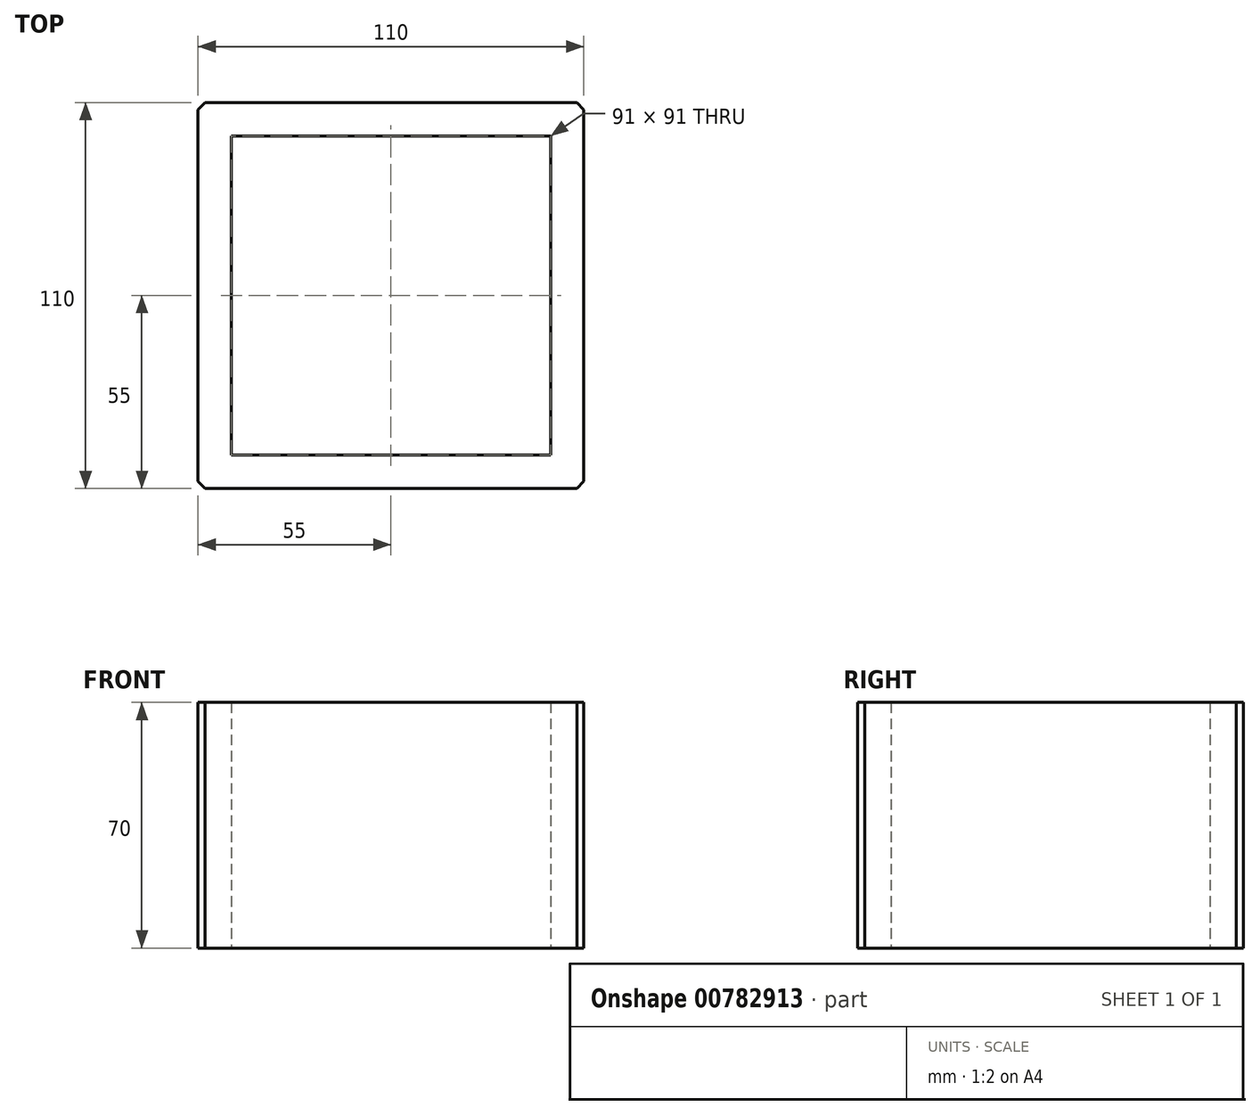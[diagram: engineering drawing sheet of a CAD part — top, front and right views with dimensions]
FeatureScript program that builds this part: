
annotation { "Feature Type Name" : "Feature", "Feature Type Description" : "" }
export const myFeature = defineFeature(function(context is Context, id is Id, definition is map)
    precondition{}
    {
        {
            var Q0;
            Q0=qCreatedBy(makeId("Top.planeOp"),FACE);
            var sketch = newSketch(context, id + "F0", { "sketchPlane" : qUnion([Q0])});
            skLineSegment(sketch, "E0.bottom", {"start": v(-55, -55) * mm, "end": v(55, -55) * mm});
            skLineSegment(sketch, "E0.top", {"start": v(-55, 55) * mm, "end": v(55, 55) * mm});
            skLineSegment(sketch, "E0.left", {"start": v(-55, -55) * mm, "end": v(-55, 55) * mm});
            skLineSegment(sketch, "E0.right", {"start": v(55, -55) * mm, "end": v(55, 55) * mm});
            skLineSegment(sketch, "E1.bottom", {"start": v(-45.5, -45.5) * mm, "end": v(45.5, -45.5) * mm});
            skLineSegment(sketch, "E1.top", {"start": v(-45.5, 45.5) * mm, "end": v(45.5, 45.5) * mm});
            skLineSegment(sketch, "E1.left", {"start": v(-45.5, -45.5) * mm, "end": v(-45.5, 45.5) * mm});
            skLineSegment(sketch, "E1.right", {"start": v(45.5, -45.5) * mm, "end": v(45.5, 45.5) * mm});
            skSolve(sketch);
        }
        {
            var Q0;
            Q0=makeQuery(id+"F0.imprint","IMPRINT",FACE,{"disambiguationData":[TD([[makeQuery(id+"F0.imprint","IMPRINT",EDGE,{"derivedFrom":sQuery(id+"F0.wireOp",EDGE,"E0.bottom")}),1.0]])]});
            extrude(context, id + "F1", {"entities" : qUnion([Q0]), "endBound" : BoundingType.SYMMETRIC, "depth" : 70 * mm, "offsetDistance" : 25 * mm});
        }
        {
            var Q0;
            Q0=makeQuery(id+"F1.opExtrude","SWEPT_EDGE",EDGE,{"disambiguationData":[OSD([sQuery(id+"F0.wireOp",EDGE,"E0.bottom"),sQuery(id+"F0.wireOp",EDGE,"E0.left")])]});
            var Q1;
            Q1=makeQuery(id+"F1.opExtrude","SWEPT_EDGE",EDGE,{"disambiguationData":[OSD([sQuery(id+"F0.wireOp",EDGE,"E0.bottom"),sQuery(id+"F0.wireOp",EDGE,"E0.right")])]});
            var Q2;
            Q2=makeQuery(id+"F1.opExtrude","SWEPT_EDGE",EDGE,{"disambiguationData":[OSD([sQuery(id+"F0.wireOp",EDGE,"E0.top"),sQuery(id+"F0.wireOp",EDGE,"E0.right")])]});
            var Q3;
            Q3=makeQuery(id+"F1.opExtrude","SWEPT_EDGE",EDGE,{"disambiguationData":[OSD([sQuery(id+"F0.wireOp",EDGE,"E0.top"),sQuery(id+"F0.wireOp",EDGE,"E0.left")])]});
            chamfer(context, id + "F2", {"entities" : qUnion([Q0, Q1, Q2, Q3]), "width" : 2 * mm, "tangentPropagation" : true});
        }
    });
